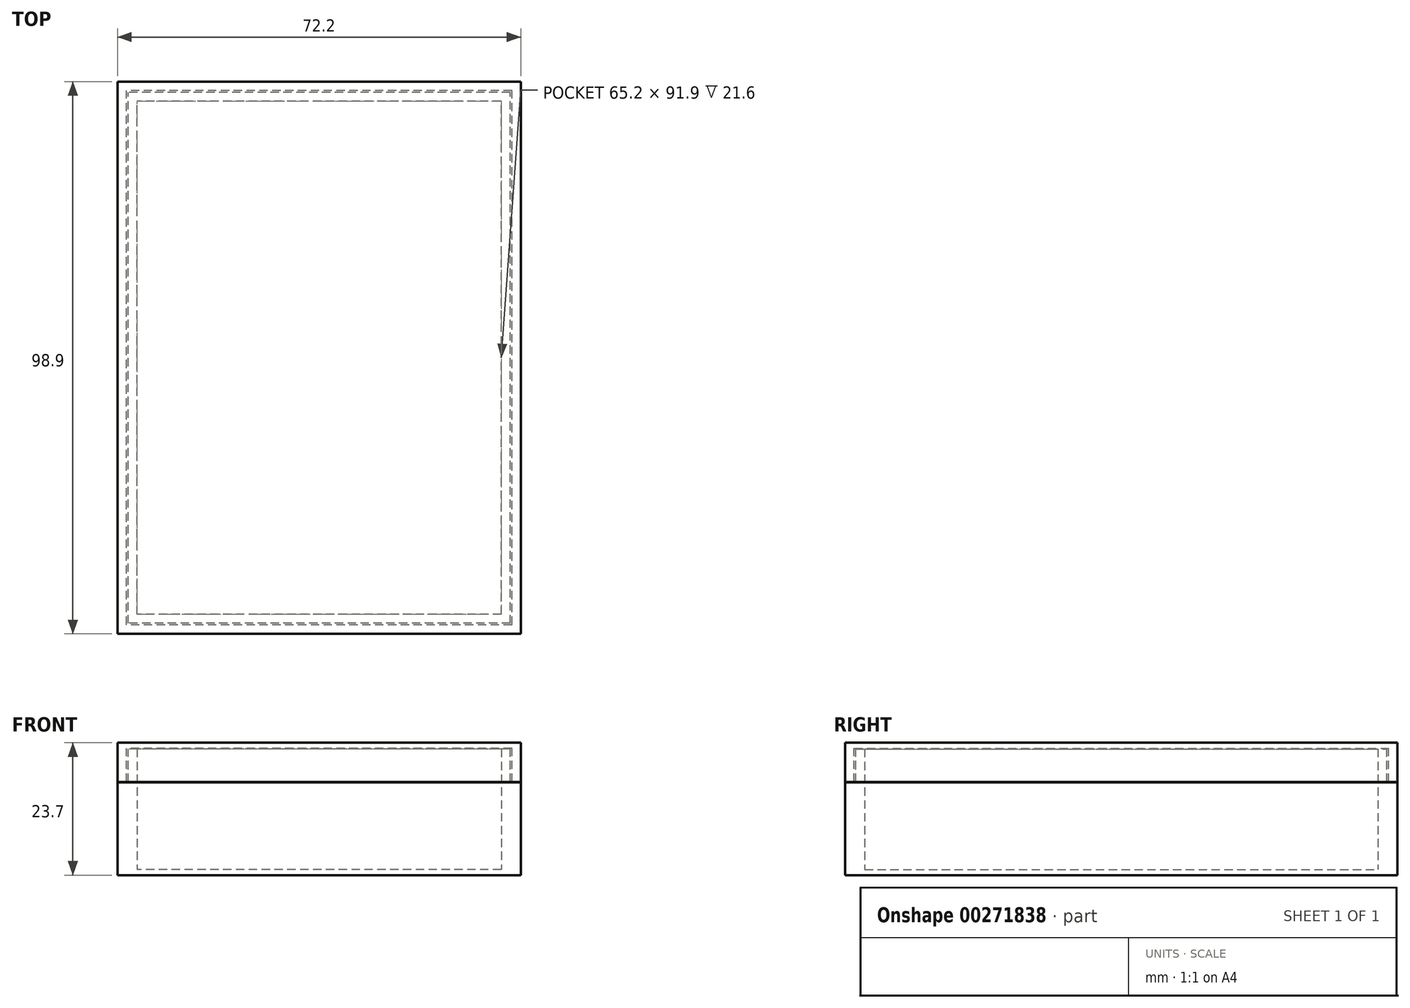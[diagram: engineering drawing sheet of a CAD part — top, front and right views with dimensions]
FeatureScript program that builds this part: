
annotation { "Feature Type Name" : "Feature", "Feature Type Description" : "" }
export const myFeature = defineFeature(function(context is Context, id is Id, definition is map)
    precondition{}
    {
        {
            assignVariable(context, id + "F0", {"name" : "chaff", "anyValue" : .3});
        }
        {
            assignVariable(context, id + "F1", {"name" : "basethick", "anyValue" : 1});
        }
        {
            assignVariable(context, id + "F2", {"name" : "deckheight", "anyValue" : 21});
        }
        {
            var Q0;
            Q0=qCreatedBy(makeId("Top.planeOp"),FACE);
            var sketch = newSketch(context, id + "F3", { "sketchPlane" : qUnion([Q0])});
            skLineSegment(sketch, "E0.bottom", {"start": v(36.1, -49.45) * mm, "end": v(-36.1, -49.45) * mm});
            skLineSegment(sketch, "E0.top", {"start": v(36.1, 49.45) * mm, "end": v(-36.1, 49.45) * mm});
            skLineSegment(sketch, "E0.left", {"start": v(36.1, -49.45) * mm, "end": v(36.1, 49.45) * mm});
            skLineSegment(sketch, "E0.right", {"start": v(-36.1, -49.45) * mm, "end": v(-36.1, 49.45) * mm});
            skPoint(sketch, "E0.middle", {"position": v(0, 0) * mm});
            skSolve(sketch);
        }
        {
            var Q0;
            Q0=qSketchRegion(id+"F3",true);
            extrude(context, id + "F4", {"entities" : qUnion([Q0]), "depth" : (getVariable(context, 'basethick')) * mm});
        }
        {
            var Q0;
            Q0=makeQuery(id+"F4.opExtrude","CAP_FACE",FACE,{"disambiguationData":[OSD([sQuery(id+"F3.wireOp",EDGE,"E0.bottom"),sQuery(id+"F3.wireOp",EDGE,"E0.top"),sQuery(id+"F3.wireOp",EDGE,"E0.left"),sQuery(id+"F3.wireOp",EDGE,"E0.right")])],"isStart":false});
            var sketch = newSketch(context, id + "F5", { "sketchPlane" : qUnion([Q0])});
            skLineSegment(sketch, "E1.bottom", {"start": v(32.6, -45.95) * mm, "end": v(-32.6, -45.95) * mm});
            skLineSegment(sketch, "E1.top", {"start": v(32.6, 45.95) * mm, "end": v(-32.6, 45.95) * mm});
            skLineSegment(sketch, "E1.left", {"start": v(32.6, -45.95) * mm, "end": v(32.6, 45.95) * mm});
            skLineSegment(sketch, "E1.right", {"start": v(-32.6, -45.95) * mm, "end": v(-32.6, 45.95) * mm});
            skPoint(sketch, "E1.middle", {"position": v(0, 0) * mm});
            skLineSegment(sketch, "E2", {"start": v(-36.1, 0) * mm, "end": v(-32.6, 0) * mm, "construction": true});
            skLineSegment(sketch, "E3", {"start": v(0, 45.95) * mm, "end": v(0, 49.45) * mm, "construction": true});
            skLineSegment(sketch, "E4.0", {"start": v(-36.1, -49.45) * mm, "end": v(-36.1, 49.45) * mm});
            skLineSegment(sketch, "E5.0", {"start": v(36.1, -49.45) * mm, "end": v(-36.1, -49.45) * mm});
            skLineSegment(sketch, "E6.0", {"start": v(36.1, -49.45) * mm, "end": v(36.1, 49.45) * mm});
            skLineSegment(sketch, "E7.0", {"start": v(36.1, 49.45) * mm, "end": v(-36.1, 49.45) * mm});
            skSolve(sketch);
        }
        {
            var Q0;
            Q0=qSketchRegion(id+"F5",true);
            extrude(context, id + "F6", {"entities" : qUnion([Q0]), "operationType" : NewBodyOperationType.ADD, "depth" : (getVariable(context, 'deckheight') + getVariable(context, 'chaff') * 2) * mm});
        }
        {
            var Q0;
            {var subQ0=sQuery(id+"FkSYW39zBoowpRB_1.wireOp",EDGE,"b7063ba6-163c-4e90-9692-3a0a1676d49b.0");var subQ1=sQuery(id+"FkSYW39zBoowpRB_1.wireOp",EDGE,"5b0bd29a-2a72-4641-92b4-ce3cebaaf724.1.0.1");var subQ2=sQuery(id+"FkSYW39zBoowpRB_1.wireOp",EDGE,"5b0bd29a-2a72-4641-92b4-ce3cebaaf724.2.0.1");Q0=makeQuery(id+"FKPirlnXY4BgwBl_1.boolean.opBoolean","MERGE",FACE,{"derivedFrom":[makeQuery(id+"F6.opExtrude","CAP_FACE",FACE,{"disambiguationData":[OSD([sQuery(id+"F5.wireOp",EDGE,"E1.bottom"),sQuery(id+"F5.wireOp",EDGE,"E1.top"),sQuery(id+"F5.wireOp",EDGE,"E1.left"),sQuery(id+"F5.wireOp",EDGE,"E1.right"),sQuery(id+"F5.wireOp",EDGE,"E4.0"),sQuery(id+"F5.wireOp",EDGE,"E5.0"),sQuery(id+"F5.wireOp",EDGE,"E6.0"),sQuery(id+"F5.wireOp",EDGE,"E7.0")])],"isStart":false}),makeQuery(id+"FKPirlnXY4BgwBl_1.opExtrude","SWEPT_FACE",FACE,{"disambiguationData":[OSD([subQ0]),TDD([makeQuery(id+"FkSYW39zBoowpRB_1.imprint","IMPRINT",EDGE,{"disambiguationData":[TD([[makeQuery(id+"FkSYW39zBoowpRB_1.imprint","INTERSECT",VERTEX,{"derivedFrom":[sQuery(id+"FkSYW39zBoowpRB_1.wireOp",EDGE,"ed8556cc-012e-414f-a647-4d99696943b9.0"),subQ0]}),-1.0]])],"derivedFrom":subQ0})])]}),makeQuery(id+"FKPirlnXY4BgwBl_1.opExtrude","SWEPT_FACE",FACE,{"disambiguationData":[OSD([subQ0]),TDD([makeQuery(id+"FkSYW39zBoowpRB_1.imprint","IMPRINT",EDGE,{"disambiguationData":[TD([[makeQuery(id+"FkSYW39zBoowpRB_1.imprint","INTERSECT",VERTEX,{"disambiguationData":[OD(1.0)],"derivedFrom":[subQ2,subQ0]}),1.0]])],"derivedFrom":subQ0})])]}),makeQuery(id+"FKPirlnXY4BgwBl_1.opExtrude","SWEPT_FACE",FACE,{"disambiguationData":[OSD([subQ0]),TDD([makeQuery(id+"FkSYW39zBoowpRB_1.imprint","IMPRINT",EDGE,{"disambiguationData":[TD([[makeQuery(id+"FkSYW39zBoowpRB_1.imprint","INTERSECT",VERTEX,{"disambiguationData":[OD(1.0)],"derivedFrom":[subQ1,subQ0]}),1.0]])],"derivedFrom":subQ0})])]}),makeQuery(id+"FKPirlnXY4BgwBl_1.opExtrude","SWEPT_FACE",FACE,{"disambiguationData":[OSD([subQ0]),TDD([makeQuery(id+"FkSYW39zBoowpRB_1.imprint","IMPRINT",EDGE,{"disambiguationData":[TD([[makeQuery(id+"FkSYW39zBoowpRB_1.imprint","INTERSECT",VERTEX,{"derivedFrom":[sQuery(id+"FkSYW39zBoowpRB_1.wireOp",EDGE,"CCxmkI6E-hdHg-CZTa-q9Gf-agiM700yoBqG"),subQ0]}),1.0]])],"derivedFrom":subQ0})])]})]});}
            cPlane(context, id + "F7", {"entities" : qUnion([Q0]), "cplaneType" : CPlaneType.OFFSET, "offset" : .1 * mm, "width" : 150 * mm, "height" : 150 * mm});
        }
        {
            var Q0;
            {var subQ0=sQuery(id+"FkSYW39zBoowpRB_1.wireOp",EDGE,"b7063ba6-163c-4e90-9692-3a0a1676d49b.0");var subQ1=sQuery(id+"FkSYW39zBoowpRB_1.wireOp",EDGE,"5b0bd29a-2a72-4641-92b4-ce3cebaaf724.1.0.1");var subQ2=sQuery(id+"FkSYW39zBoowpRB_1.wireOp",EDGE,"5b0bd29a-2a72-4641-92b4-ce3cebaaf724.2.0.1");Q0=makeQuery(id+"FKPirlnXY4BgwBl_1.boolean.opBoolean","MERGE",FACE,{"derivedFrom":[makeQuery(id+"F6.opExtrude","CAP_FACE",FACE,{"disambiguationData":[OSD([sQuery(id+"F5.wireOp",EDGE,"E1.bottom"),sQuery(id+"F5.wireOp",EDGE,"E1.top"),sQuery(id+"F5.wireOp",EDGE,"E1.left"),sQuery(id+"F5.wireOp",EDGE,"E1.right"),sQuery(id+"F5.wireOp",EDGE,"E4.0"),sQuery(id+"F5.wireOp",EDGE,"E5.0"),sQuery(id+"F5.wireOp",EDGE,"E6.0"),sQuery(id+"F5.wireOp",EDGE,"E7.0")])],"isStart":false}),makeQuery(id+"FKPirlnXY4BgwBl_1.opExtrude","SWEPT_FACE",FACE,{"disambiguationData":[OSD([subQ0]),TDD([makeQuery(id+"FkSYW39zBoowpRB_1.imprint","IMPRINT",EDGE,{"disambiguationData":[TD([[makeQuery(id+"FkSYW39zBoowpRB_1.imprint","INTERSECT",VERTEX,{"derivedFrom":[sQuery(id+"FkSYW39zBoowpRB_1.wireOp",EDGE,"ed8556cc-012e-414f-a647-4d99696943b9.0"),subQ0]}),-1.0]])],"derivedFrom":subQ0})])]}),makeQuery(id+"FKPirlnXY4BgwBl_1.opExtrude","SWEPT_FACE",FACE,{"disambiguationData":[OSD([subQ0]),TDD([makeQuery(id+"FkSYW39zBoowpRB_1.imprint","IMPRINT",EDGE,{"disambiguationData":[TD([[makeQuery(id+"FkSYW39zBoowpRB_1.imprint","INTERSECT",VERTEX,{"disambiguationData":[OD(1.0)],"derivedFrom":[subQ2,subQ0]}),1.0]])],"derivedFrom":subQ0})])]}),makeQuery(id+"FKPirlnXY4BgwBl_1.opExtrude","SWEPT_FACE",FACE,{"disambiguationData":[OSD([subQ0]),TDD([makeQuery(id+"FkSYW39zBoowpRB_1.imprint","IMPRINT",EDGE,{"disambiguationData":[TD([[makeQuery(id+"FkSYW39zBoowpRB_1.imprint","INTERSECT",VERTEX,{"disambiguationData":[OD(1.0)],"derivedFrom":[subQ1,subQ0]}),1.0]])],"derivedFrom":subQ0})])]}),makeQuery(id+"FKPirlnXY4BgwBl_1.opExtrude","SWEPT_FACE",FACE,{"disambiguationData":[OSD([subQ0]),TDD([makeQuery(id+"FkSYW39zBoowpRB_1.imprint","IMPRINT",EDGE,{"disambiguationData":[TD([[makeQuery(id+"FkSYW39zBoowpRB_1.imprint","INTERSECT",VERTEX,{"derivedFrom":[sQuery(id+"FkSYW39zBoowpRB_1.wireOp",EDGE,"CCxmkI6E-hdHg-CZTa-q9Gf-agiM700yoBqG"),subQ0]}),1.0]])],"derivedFrom":subQ0})])]})]});}
            var sketch = newSketch(context, id + "F8", { "sketchPlane" : qUnion([Q0])});
            skLineSegment(sketch, "E8.0", {"start": v(36.1, 49.45) * mm, "end": v(-36.1, 49.45) * mm});
            skLineSegment(sketch, "E9.0", {"start": v(-36.1, -49.45) * mm, "end": v(-36.1, 49.45) * mm});
            skLineSegment(sketch, "E10.0", {"start": v(36.1, -49.45) * mm, "end": v(-36.1, -49.45) * mm});
            skLineSegment(sketch, "E11.0", {"start": v(36.1, -49.45) * mm, "end": v(36.1, 49.45) * mm});
            skLineSegment(sketch, "E12.0", {"start": v(34.2, 47.55) * mm, "end": v(-34.2, 47.55) * mm});
            skLineSegment(sketch, "E12.1", {"start": v(34.2, -47.55) * mm, "end": v(34.2, 47.55) * mm});
            skLineSegment(sketch, "E12.2", {"start": v(34.2, -47.55) * mm, "end": v(-34.2, -47.55) * mm});
            skLineSegment(sketch, "E12.3", {"start": v(-34.2, -47.55) * mm, "end": v(-34.2, 47.55) * mm});
            skSolve(sketch);
        }
        {
            var Q0;
            Q0=makeQuery(id+"F8.imprint","IMPRINT",FACE,{"disambiguationData":[TD([[makeQuery(id+"F8.imprint","IMPRINT",EDGE,{"derivedFrom":sQuery(id+"F8.wireOp",EDGE,"E8.0")}),1.0]])]});
            extrude(context, id + "F9", {"entities" : qUnion([Q0]), "operationType" : NewBodyOperationType.REMOVE, "oppositeDirection" : true, "depth" : 6 * mm});
        }
        {
            var Q0;
            Q0=qCreatedBy(id+"F7.planeOp",FACE);
            var sketch = newSketch(context, id + "F10", { "sketchPlane" : qUnion([Q0])});
            skLineSegment(sketch, "E13.0", {"start": v(-36.1, -49.45) * mm, "end": v(-36.1, 49.45) * mm});
            skLineSegment(sketch, "E14.0", {"start": v(36.1, -49.45) * mm, "end": v(-36.1, -49.45) * mm});
            skLineSegment(sketch, "E15.0", {"start": v(36.1, 49.45) * mm, "end": v(-36.1, 49.45) * mm});
            skLineSegment(sketch, "E16.0", {"start": v(36.1, -49.45) * mm, "end": v(36.1, 49.45) * mm});
            skSolve(sketch);
        }
        {
            var Q0;
            Q0 = qSketchRegion(id + "F10", true);
            extrude(context, id + "F11", {"entities" : qUnion([Q0]), "depth" : (getVariable(context, 'basethick')) * mm});
        }
        {
            var Q0;
            Q0=makeQuery(id+"F11.opExtrude","CAP_FACE",FACE,{"disambiguationData":[OSD([sQuery(id+"F10.wireOp",EDGE,"E13.0"),sQuery(id+"F10.wireOp",EDGE,"E14.0"),sQuery(id+"F10.wireOp",EDGE,"E15.0"),sQuery(id+"F10.wireOp",EDGE,"E16.0")])],"isStart":true});
            var sketch = newSketch(context, id + "F12", { "sketchPlane" : qUnion([Q0])});
            skLineSegment(sketch, "E17.0", {"start": v(36.1, 49.45) * mm, "end": v(36.1, -49.45) * mm});
            skLineSegment(sketch, "E18.0", {"start": v(36.1, 49.45) * mm, "end": v(-36.1, 49.45) * mm});
            skLineSegment(sketch, "E19.0", {"start": v(36.1, -49.45) * mm, "end": v(-36.1, -49.45) * mm});
            skLineSegment(sketch, "E20.0", {"start": v(-36.1, 49.45) * mm, "end": v(-36.1, -49.45) * mm});
            skLineSegment(sketch, "E21.0", {"start": v(34.5, 47.85) * mm, "end": v(34.5, -47.85) * mm});
            skLineSegment(sketch, "E21.1", {"start": v(34.5, 47.85) * mm, "end": v(-34.5, 47.85) * mm});
            skLineSegment(sketch, "E21.2", {"start": v(-34.5, 47.85) * mm, "end": v(-34.5, -47.85) * mm});
            skLineSegment(sketch, "E21.3", {"start": v(34.5, -47.85) * mm, "end": v(-34.5, -47.85) * mm});
            skSolve(sketch);
        }
        {
            var Q0;
            Q0 = qSketchRegion(id + "F12", true);
            extrude(context, id + "F13", {"entities" : qUnion([Q0]), "operationType" : NewBodyOperationType.ADD, "depth" : 6 * mm});
        }
    });
